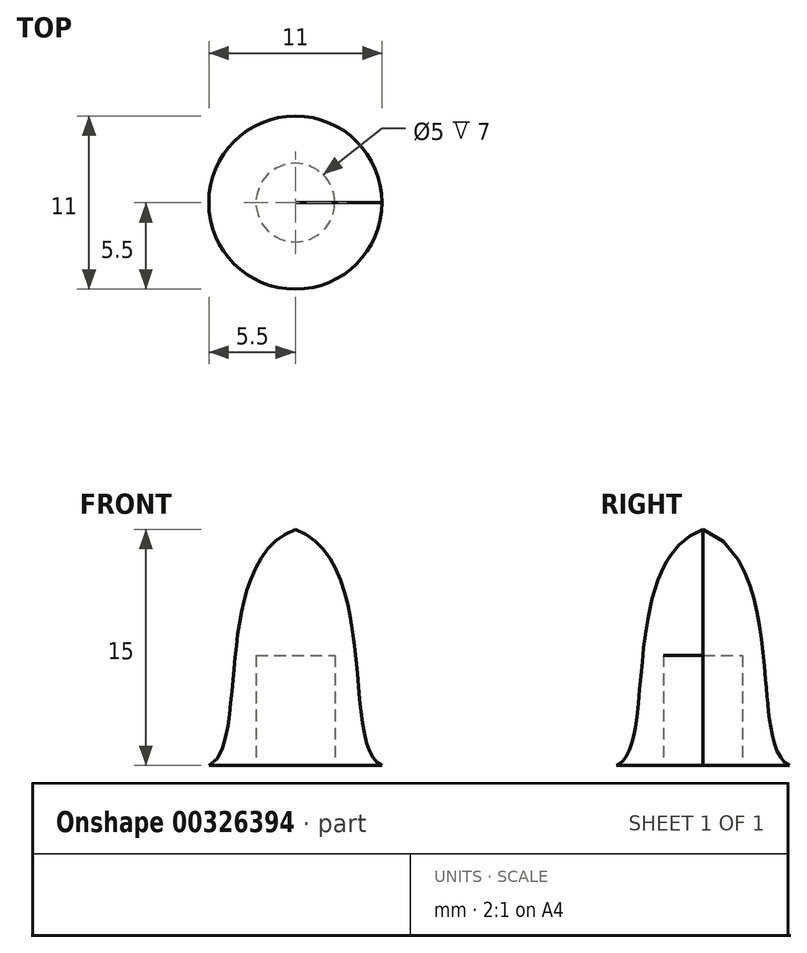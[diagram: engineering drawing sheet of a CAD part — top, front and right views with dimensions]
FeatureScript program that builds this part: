
annotation { "Feature Type Name" : "Feature", "Feature Type Description" : "" }
export const myFeature = defineFeature(function(context is Context, id is Id, definition is map)
    precondition{}
    {
        {
            var Q0;
            Q0=qCreatedBy(makeId("Front.planeOp"),FACE);
            var sketch = newSketch(context, id + "F0", { "sketchPlane" : qUnion([Q0])});
            skLineSegment(sketch, "E0.rect.bottom", {"start": v(0, -7.5) * mm, "end": v(-3, -7.5) * mm});
            skLineSegment(sketch, "E0.rect.right", {"start": v(-5.5, -0.5) * mm, "end": v(-5.5, 7.5) * mm});
            skPoint(sketch, "E0.rect.middle", {"position": v(-2.75, 0) * mm});
            skFitSpline(sketch, "E1", {"points": [v(-5.5, 7.5) * mm, v(0, -7.5) * mm], "startDerivative": vector(16.36, -6.03) * mm, "endDerivative": vector(7.94, -3.3) * mm});
            skLineSegment(sketch, "E2.top", {"start": v(-5.5, -0.5) * mm, "end": v(-3, -0.5) * mm});
            skLineSegment(sketch, "E2.right", {"start": v(-3, -7.5) * mm, "end": v(-3, -0.5) * mm});
            skPoint(sketch, "E0.rect.top.start.orphan", {"position": v(0, 7.5) * mm});
            skPoint(sketch, "E2.bottom.start.orphan", {"position": v(-5.5, -7.5) * mm});
            skSolve(sketch);
        }
        {
            var Q0;
            Q0=qSketchRegion(id+"F0",true);
            var Q1;
            Q1=sQuery(id+"F0.wireOp",EDGE,"E0.rect.right");
            revolve(context, id + "F1", {"entities" : qUnion([Q0]), "axis" : qUnion([Q1]), "revolveType" : RevolveType.FULL});
        }
    });
